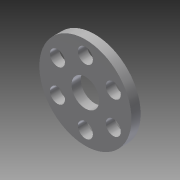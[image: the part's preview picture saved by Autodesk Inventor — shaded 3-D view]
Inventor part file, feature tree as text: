
AUTODESK INVENTOR PART (.ipt)
format: ipt  version: 2013 (Build 170138000, 138)  size: 99,328 bytes
history: native  units: in
note: dims shown in document units (in); Inventor stores cm internally (conversion verified against a paired STEP export)
features: extrude x1, sketch x1
ambient origin geometry x8: Origin, YZ Plane, XZ Plane, XY Plane, X Axis, Y Axis, Z Axis, Center Point
bodies: Solid1 (feature_tree)
feature tree (2):
  extrude  "Extrusion1"  Depth=1.25in
  sketch  "Sketch1"  dims[d0=0.375in d1=1.25in d2=0.25in d3=0.204in d4=2.3622in d6=360.0deg d8=0.125in d9=0.0in]
